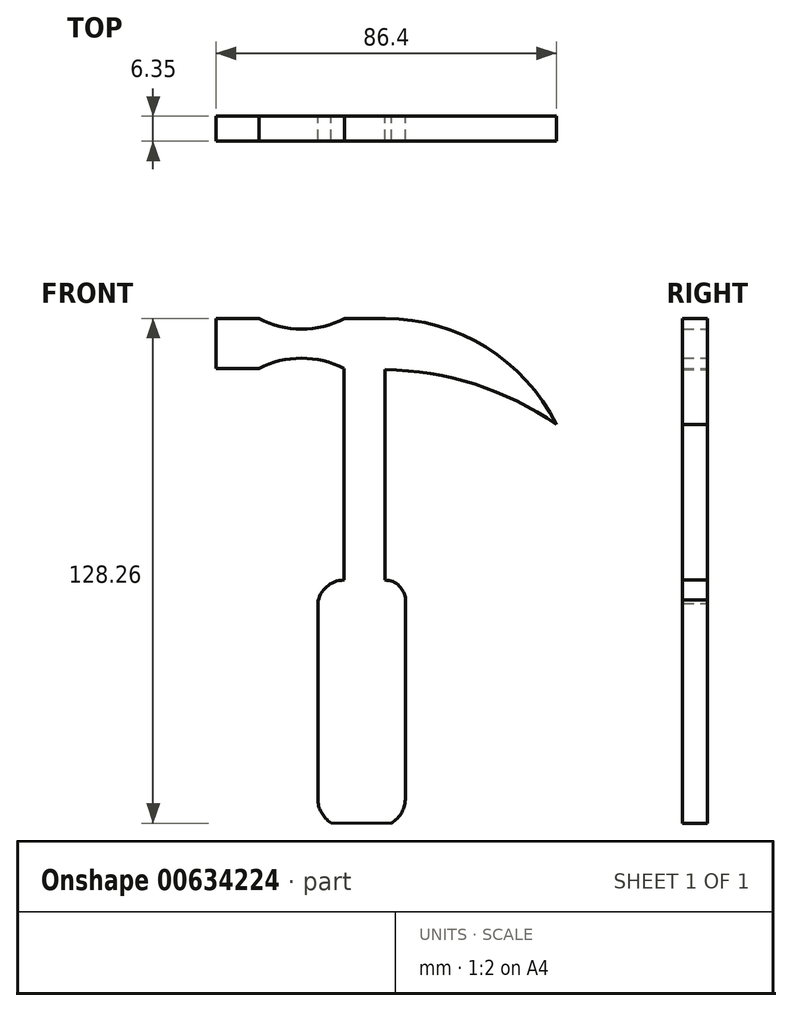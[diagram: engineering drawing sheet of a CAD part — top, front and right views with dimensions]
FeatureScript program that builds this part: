
annotation { "Feature Type Name" : "Feature", "Feature Type Description" : "" }
export const myFeature = defineFeature(function(context is Context, id is Id, definition is map)
    precondition{}
    {
        {
            var Q0;
            Q0=qCreatedBy(makeId("Front.planeOp"),FACE);
            var sketch = newSketch(context, id + "F0", { "sketchPlane" : qUnion([Q0])});
            skLineSegment(sketch, "E0", {"start": v(-55.24, 52.88) * mm, "end": v(-44.38, 52.88) * mm});
            skLineSegment(sketch, "E1", {"start": v(-44.38, 52.88) * mm, "end": v(-44.38, 40.13) * mm});
            skLineSegment(sketch, "E2", {"start": v(-44.38, 40.13) * mm, "end": v(-55.24, 40.13) * mm});
            skLineSegment(sketch, "E3", {"start": v(-55.24, 40.13) * mm, "end": v(-55.24, 52.88) * mm});
            skArc(sketch, "E4", {"start": v(-44.38, 52.88) * mm, "mid": v(-33.52, 50.12) * mm, "end": v(-22.66, 52.88) * mm});
            skLineSegment(sketch, "E5.right", {"start": v(-12.28, 52.88) * mm, "end": v(-12.32, 39.85) * mm});
            skArc(sketch, "E6", {"start": v(31.16, 25.97) * mm, "mid": v(13.27, 45.6) * mm, "end": v(-12.28, 52.88) * mm});
            skArc(sketch, "E7", {"start": v(31.16, 25.97) * mm, "mid": v(10.46, 36.16) * mm, "end": v(-12.32, 39.85) * mm});
            skArc(sketch, "E8", {"start": v(-22.79, 40.13) * mm, "mid": v(-33.59, 42.78) * mm, "end": v(-44.38, 40.13) * mm});
            skLineSegment(sketch, "E9", {"start": v(-22.66, 52.88) * mm, "end": v(-22.79, 40.13) * mm});
            skLineSegment(sketch, "E10", {"start": v(-22.66, 52.88) * mm, "end": v(-12.28, 52.88) * mm});
            skLineSegment(sketch, "E11", {"start": v(-22.79, 40.13) * mm, "end": v(-12.32, 39.85) * mm});
            skLineSegment(sketch, "E12", {"start": v(-22.79, 40.13) * mm, "end": v(-22.79, -13.63) * mm});
            skLineSegment(sketch, "E13", {"start": v(-12.32, 39.85) * mm, "end": v(-12.32, -13.63) * mm});
            skLineSegment(sketch, "E14", {"start": v(-22.79, -13.63) * mm, "end": v(-12.32, -13.63) * mm});
            skArc(sketch, "E15", {"start": v(-22.79, -13.63) * mm, "mid": v(-27.22, -15.3) * mm, "end": v(-29.41, -19.5) * mm});
            skArc(sketch, "E16", {"start": v(-7.16, -18.6) * mm, "mid": v(-8.74, -15.07) * mm, "end": v(-12.32, -13.63) * mm});
            skLineSegment(sketch, "E17", {"start": v(-29.41, -19.5) * mm, "end": v(-29.41, -69.19) * mm});
            skLineSegment(sketch, "E18", {"start": v(-7.16, -18.6) * mm, "end": v(-7.16, -68.88) * mm});
            skArc(sketch, "E19", {"start": v(-29.41, -69.19) * mm, "mid": v(-28.52, -72.67) * mm, "end": v(-26.06, -75.29) * mm});
            skArc(sketch, "E20", {"start": v(-10.67, -75.38) * mm, "mid": v(-8.1, -72.57) * mm, "end": v(-7.16, -68.88) * mm});
            skLineSegment(sketch, "E21", {"start": v(-26.06, -75.29) * mm, "end": v(-10.67, -75.38) * mm});
            skSolve(sketch);
        }
        {
            var Q0;
            Q0 = qSketchRegion(id + "F0", true);
            extrude(context, id + "F1", {"entities" : qUnion([Q0]), "depth" : 6.35 * mm, "offsetDistance" : 25.4 * mm});
        }
    });
